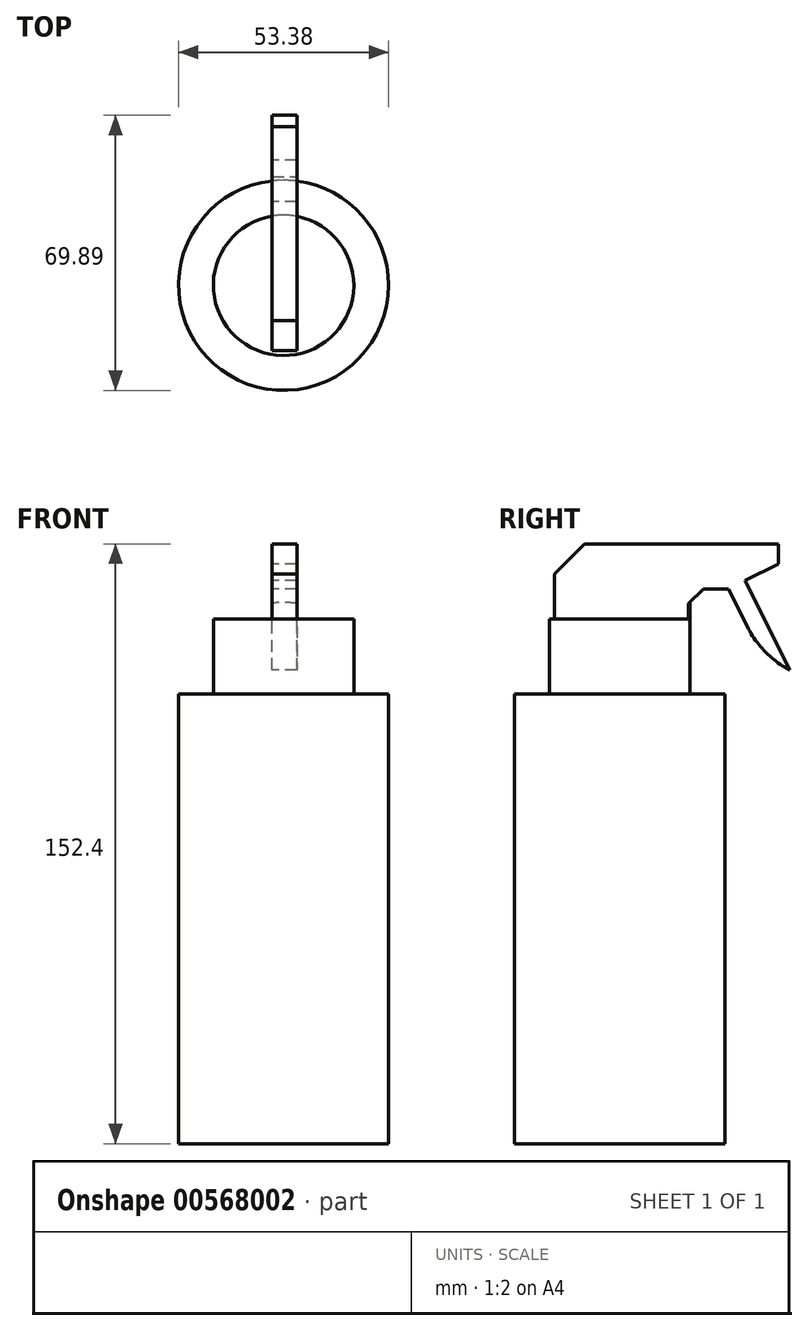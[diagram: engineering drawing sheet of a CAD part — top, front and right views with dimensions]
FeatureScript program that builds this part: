
annotation { "Feature Type Name" : "Feature", "Feature Type Description" : "" }
export const myFeature = defineFeature(function(context is Context, id is Id, definition is map)
    precondition{}
    {
        {
            var Q0;
            Q0=qCreatedBy(makeId("Top.planeOp"),FACE);
            var sketch = newSketch(context, id + "F0", { "sketchPlane" : qUnion([Q0])});
            skCircle(sketch, "E0", {"center": v(0, 0) * mm, "radius": 26.69 * mm});
            skSolve(sketch);
        }
        {
            var Q0;
            Q0 = qSketchRegion(id + "F0", true);
            extrude(context, id + "F1", {"entities" : qUnion([Q0]), "depth" : 114.3 * mm, "offsetDistance" : 25.4 * mm});
        }
        {
            var Q0;
            Q0=makeQuery(id+"F1.opExtrude","CAP_FACE",FACE,{"disambiguationData":[OSD([sQuery(id+"F0.wireOp",EDGE,"E0")])],"isStart":false});
            var sketch = newSketch(context, id + "F2", { "sketchPlane" : qUnion([Q0])});
            skCircle(sketch, "E1", {"center": v(0, 0) * mm, "radius": 17.85 * mm});
            skSolve(sketch);
        }
        {
            var Q0;
            Q0 = qSketchRegion(id + "F2", true);
            extrude(context, id + "F3", {"entities" : qUnion([Q0]), "operationType" : NewBodyOperationType.ADD, "depth" : 19.05 * mm, "offsetDistance" : 25.4 * mm});
        }
        {
            var Q0;
            Q0=makeQuery(id+"F3.opExtrude","CAP_FACE",FACE,{"disambiguationData":[OSD([sQuery(id+"F2.wireOp",EDGE,"E1")])],"isStart":false});
            var sketch = newSketch(context, id + "F4", { "sketchPlane" : qUnion([Q0])});
            skCircle(sketch, "E2", {"center": v(0, 0) * mm, "radius": 14.64 * mm});
            skSolve(sketch);
        }
        {
            var Q0;
            Q0 = qSketchRegion(id + "F4", true);
            var sketch = newSketch(context, id + "F5", { "sketchPlane" : qUnion([Q0])});
            skLineSegment(sketch, "E3.bottom", {"start": v(3.4, -16.62) * mm, "end": v(-2.93, -16.62) * mm});
            skLineSegment(sketch, "E3.top", {"start": v(3.4, 21.28) * mm, "end": v(-2.93, 21.28) * mm});
            skLineSegment(sketch, "E3.left", {"start": v(3.4, -16.62) * mm, "end": v(3.4, 21.28) * mm});
            skLineSegment(sketch, "E3.right", {"start": v(-2.93, -16.62) * mm, "end": v(-2.93, 21.28) * mm});
            skSolve(sketch);
        }
        {
            var Q0;
            Q0 = qSketchRegion(id + "F5", true);
            extrude(context, id + "F6", {"entities" : qUnion([Q0]), "operationType" : NewBodyOperationType.ADD, "depth" : 19.05 * mm, "offsetDistance" : 25.4 * mm});
        }
        {
            var Q0;
            Q0=makeQuery(id+"F6.opExtrude","CAP_EDGE",EDGE,{"disambiguationData":[OSD([sQuery(id+"F5.wireOp",EDGE,"E3.bottom")])],"isStart":false});
            var Q1;
            Q1=makeQuery(id+"F6.opExtrude","CAP_EDGE",EDGE,{"disambiguationData":[OSD([sQuery(id+"F5.wireOp",EDGE,"E3.top")])],"isStart":true});
            chamfer(context, id + "F7", {"entities" : qUnion([Q0, Q1]), "width" : 7.62 * mm, "tangentPropagation" : true});
        }
        {
            var Q0;
            Q0=makeQuery(id+"F6.opExtrude","SWEPT_FACE",FACE,{"disambiguationData":[OSD([sQuery(id+"F5.wireOp",EDGE,"E3.top")])]});
            var sketch = newSketch(context, id + "F8", { "sketchPlane" : qUnion([Q0])});
            skLineSegment(sketch, "E4.bottom", {"start": v(-3.4, 140.97) * mm, "end": v(2.93, 140.97) * mm});
            skLineSegment(sketch, "E4.top", {"start": v(-3.4, 152.4) * mm, "end": v(2.93, 152.4) * mm});
            skLineSegment(sketch, "E4.left", {"start": v(-3.4, 140.97) * mm, "end": v(-3.4, 152.4) * mm});
            skLineSegment(sketch, "E4.right", {"start": v(2.93, 140.97) * mm, "end": v(2.93, 152.4) * mm});
            skSolve(sketch);
        }
        {
            var Q0;
            Q0 = qSketchRegion(id + "F8", true);
            extrude(context, id + "F9", {"entities" : qUnion([Q0]), "operationType" : NewBodyOperationType.ADD, "depth" : 19.05 * mm, "offsetDistance" : 25.4 * mm});
        }
        {
            var Q0;
            Q0=makeQuery(id+"F9.opExtrude","CAP_EDGE",EDGE,{"disambiguationData":[OSD([sQuery(id+"F8.wireOp",EDGE,"E4.bottom")])],"isStart":false});
            chamfer(context, id + "F10", {"entities" : qUnion([Q0]), "chamferType" : ChamferType.TWO_OFFSETS, "width1" : 6.35 * mm, "oppositeDirection" : false, "width2" : 12.7 * mm, "tangentPropagation" : true});
        }
        {
            var Q0;
            Q0=makeQuery(id+"F10.opChamfer","BLEND_FACE",FACE,{"disambiguationData":[OSD([sQuery(id+"F8.wireOp",EDGE,"E4.bottom")])]});
            var sketch = newSketch(context, id + "F11", { "sketchPlane" : qUnion([Q0])});
            skLineSegment(sketch, "E5", {"start": v(3.4, -92.47) * mm, "end": v(-2.93, -92.47) * mm});
            skSolve(sketch);
        }
        {
            var Q0;
            {var subQ0=sQuery(id+"F11.wireOp",EDGE,"E5");Q0=makeQuery(id+"F11.imprint","IMPRINT",FACE,{"disambiguationData":[TD([[makeQuery(id+"F11.imprint","IMPRINT",EDGE,{"derivedFrom":subQ0}),-1.0]])]});}
            extrude(context, id + "F12", {"entities" : qUnion([Q0]), "operationType" : NewBodyOperationType.ADD, "depth" : 25.4 * mm, "offsetDistance" : 25.4 * mm});
        }
        {
            var Q0;
            Q0=makeQuery(id+"F12.opExtrude","CAP_EDGE",EDGE,{"disambiguationData":[OSD([sQuery(id+"F8.wireOp",EDGE,"E4.bottom")])],"isStart":false});
            fillet(context, id + "F13", {"entities" : qUnion([Q0]), "radius" : 25.4 * mm, "tangentPropagation" : true, "rho" : 0.5, "crossSection" : FilletCrossSection.CONIC, "allowEdgeOverflow" : false});
        }
    });
